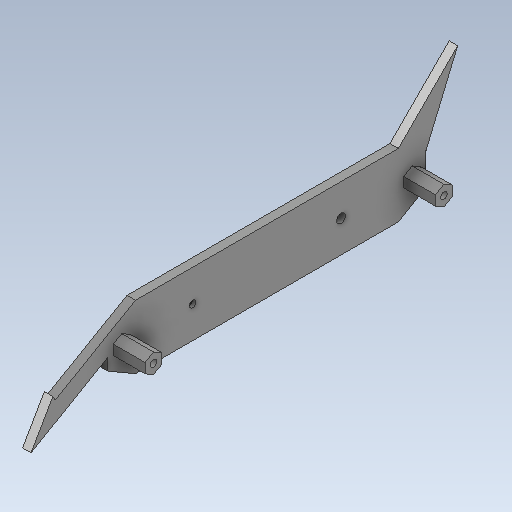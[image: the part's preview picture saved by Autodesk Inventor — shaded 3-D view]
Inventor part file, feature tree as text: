
AUTODESK INVENTOR PART (.ipt)
format: ipt  version: 2020 (Build 240168000, 168)  size: 177,152 bytes
history: native  units: in
note: dims shown in document units (in); Inventor stores cm internally (conversion verified against a paired STEP export)
features: other x3, extrude x2, sketch x2
ambient origin geometry x8: Origin, YZ Plane, XZ Plane, XY Plane, X Axis, Y Axis, Z Axis, Center Point
bodies: Solid1 (feature_tree)
feature tree (7):
  other  "HexWheelGuard.ipt"
  extrude  "Extrusion1"  TaperAngle=0.0deg  [1 undecoded]
  extrude  "Extrusion2"  Depth=0.5906in
  other  "Solid1::HexWheelGuard.ipt"
  other  "TaggingFeature1"
  sketch  "Sketch1"  dims[d0=0.3937in d6=0.0in d7=0.0in]
  sketch  "Sketch2"  dims[d9=0.315in d10=1.4843in d11=60.0deg d12=0.0787in d13=0.3937in d14=0.0in d20=0.3937in d21=0.5906in d22=1.1024in]
note: 1 required parameter value undecoded (feature->parameter linkage not recoverable at this tier; creation-order binding heuristic only, values carry confidence <= 0.55)
